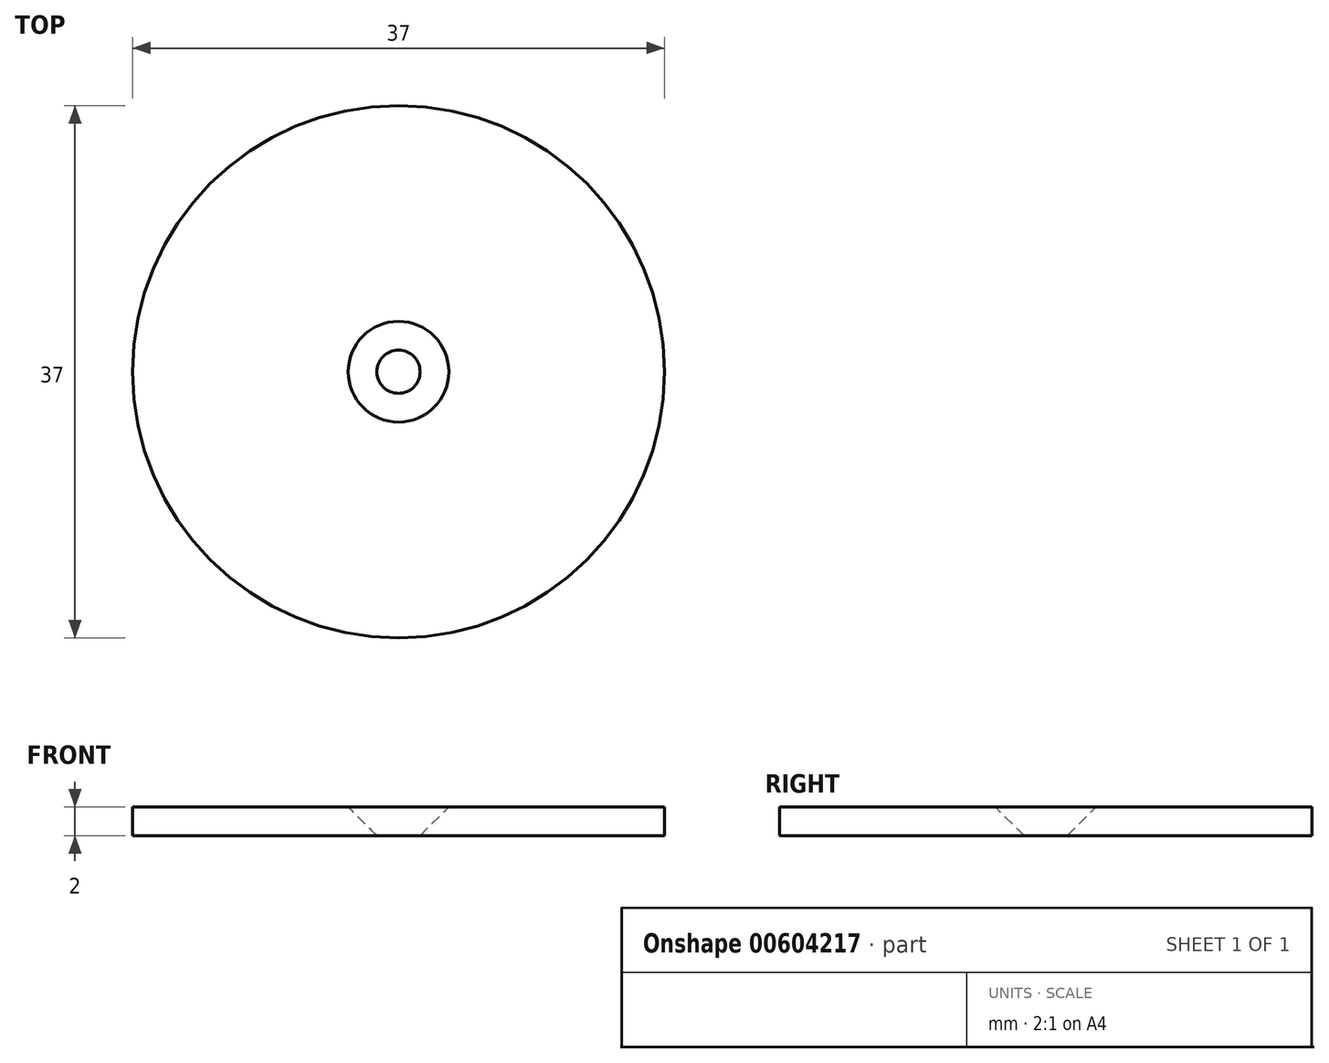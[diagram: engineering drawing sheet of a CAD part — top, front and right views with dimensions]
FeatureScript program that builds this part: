
annotation { "Feature Type Name" : "Feature", "Feature Type Description" : "" }
export const myFeature = defineFeature(function(context is Context, id is Id, definition is map)
    precondition{}
    {
        {
            var Q0;
            Q0=qCreatedBy(makeId("Front.planeOp"),FACE);
            var sketch = newSketch(context, id + "F0", { "sketchPlane" : qUnion([Q0])});
            skLineSegment(sketch, "E0", {"start": v(1.5, 0) * mm, "end": v(18.5, 0) * mm});
            skLineSegment(sketch, "E1", {"start": v(18.5, 0) * mm, "end": v(18.5, 2) * mm});
            skLineSegment(sketch, "E2", {"start": v(18.5, 2) * mm, "end": v(3.5, 2) * mm});
            skLineSegment(sketch, "E3", {"start": v(3.5, 2) * mm, "end": v(1.5, 0) * mm});
            skLineSegment(sketch, "E4", {"start": v(0, 0) * mm, "end": v(0, 17.8) * mm, "construction": true});
            skSolve(sketch);
        }
        {
            var Q0;
            Q0=makeQuery(id+"F0.imprint","IMPRINT",FACE,{"disambiguationData":[TD([[makeQuery(id+"F0.imprint","IMPRINT",EDGE,{"derivedFrom":sQuery(id+"F0.wireOp",EDGE,"E0")}),1.0]])]});
            var Q1;
            Q1=sQuery(id+"F0.wireOp",EDGE,"E4");
            revolve(context, id + "F1", {"entities" : qUnion([Q0]), "axis" : qUnion([Q1]), "revolveType" : RevolveType.FULL});
        }
    });
